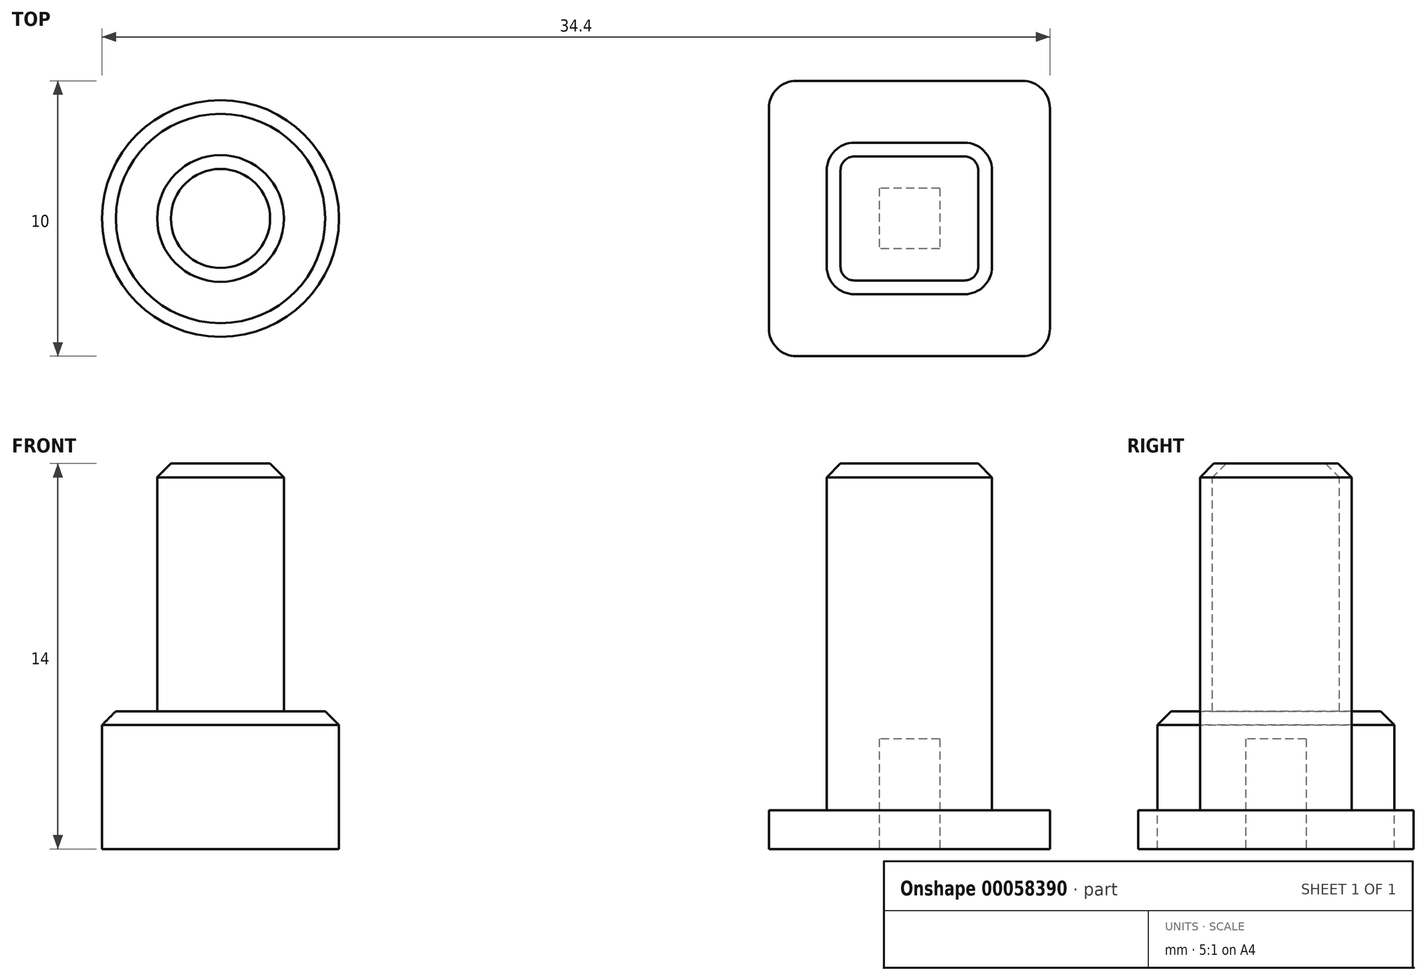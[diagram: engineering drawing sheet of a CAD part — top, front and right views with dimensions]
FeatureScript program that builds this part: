
annotation { "Feature Type Name" : "Feature", "Feature Type Description" : "" }
export const myFeature = defineFeature(function(context is Context, id is Id, definition is map)
    precondition{}
    {
        {
            var Q0;
            Q0=qCreatedBy(makeId("Front.planeOp"),FACE);
            var sketch = newSketch(context, id + "F0", { "sketchPlane" : qUnion([Q0])});
            skLineSegment(sketch, "E0", {"start": v(0, 0) * mm, "end": v(-4.3, 0) * mm});
            skLineSegment(sketch, "E1", {"start": v(-4.3, 5) * mm, "end": v(-2.3, 5) * mm});
            skLineSegment(sketch, "E2", {"start": v(-2.3, 5) * mm, "end": v(-2.3, 14) * mm});
            skLineSegment(sketch, "E3", {"start": v(-2.3, 14) * mm, "end": v(0, 14) * mm});
            skLineSegment(sketch, "E4", {"start": v(0, 14) * mm, "end": v(0, 0) * mm});
            skLineSegment(sketch, "E5", {"start": v(-4.3, 0) * mm, "end": v(-4.3, 5) * mm});
            skSolve(sketch);
        }
        {
            var Q0;
            Q0=makeQuery(id+"F0.imprint","IMPRINT",FACE,{"disambiguationData":[TD([[makeQuery(id+"F0.imprint","IMPRINT",EDGE,{"derivedFrom":sQuery(id+"F0.wireOp",EDGE,"E0")}),-1.0]])]});
            var Q1;
            Q1=sQuery(id+"F0.wireOp",EDGE,"E4");
            revolve(context, id + "F1", {"entities" : qUnion([Q0]), "axis" : qUnion([Q1]), "revolveType" : RevolveType.FULL});
        }
        {
            var Q0;
            Q0=makeQuery(id+"F1.opRevolve","SWEPT_EDGE",EDGE,{"disambiguationData":[OSD([sQuery(id+"F0.wireOp",EDGE,"E1"),sQuery(id+"F0.wireOp",EDGE,"E5")])]});
            var Q1;
            Q1=makeQuery(id+"F1.opRevolve","SWEPT_EDGE",EDGE,{"disambiguationData":[OSD([sQuery(id+"F0.wireOp",EDGE,"E2"),sQuery(id+"F0.wireOp",EDGE,"E3")])]});
            chamfer(context, id + "F2", {"entities" : qUnion([Q0, Q1]), "width" : 0.5 * mm, "tangentPropagation" : true});
        }
        {
            var Q0;
            Q0=qCreatedBy(makeId("Top.planeOp"),FACE);
            var sketch = newSketch(context, id + "F3", { "sketchPlane" : qUnion([Q0])});
            skLineSegment(sketch, "E6.rect.bottom", {"start": v(26.1, 1.1) * mm, "end": v(23.9, 1.1) * mm});
            skLineSegment(sketch, "E6.rect.top", {"start": v(26.1, -1.1) * mm, "end": v(23.9, -1.1) * mm});
            skLineSegment(sketch, "E6.rect.left", {"start": v(26.1, 1.1) * mm, "end": v(26.1, -1.1) * mm});
            skLineSegment(sketch, "E6.rect.right", {"start": v(23.9, 1.1) * mm, "end": v(23.9, -1.1) * mm});
            skPoint(sketch, "E6.rect.middle", {"position": v(25, 0) * mm});
            skLineSegment(sketch, "E7.rect.bottom", {"start": v(22, 2.75) * mm, "end": v(28, 2.75) * mm});
            skLineSegment(sketch, "E7.rect.top", {"start": v(22, -2.75) * mm, "end": v(28, -2.75) * mm});
            skLineSegment(sketch, "E7.rect.left", {"start": v(22, 2.75) * mm, "end": v(22, -2.75) * mm});
            skLineSegment(sketch, "E7.rect.right", {"start": v(28, 2.75) * mm, "end": v(28, -2.75) * mm});
            skLineSegment(sketch, "E8.rect.bottom", {"start": v(19.9, 5) * mm, "end": v(30.1, 5) * mm});
            skLineSegment(sketch, "E8.rect.top", {"start": v(19.9, -5) * mm, "end": v(30.1, -5) * mm});
            skLineSegment(sketch, "E8.rect.left", {"start": v(19.9, 5) * mm, "end": v(19.9, -5) * mm});
            skLineSegment(sketch, "E8.rect.right", {"start": v(30.1, 5) * mm, "end": v(30.1, -5) * mm});
            skSolve(sketch);
        }
        {
            var Q0;
            Q0=makeQuery(id+"F3.imprint","IMPRINT",FACE,{"disambiguationData":[TD([[makeQuery(id+"F3.imprint","IMPRINT",EDGE,{"derivedFrom":sQuery(id+"F3.wireOp",EDGE,"E6.rect.bottom")}),1.0]])]});
            var Q1;
            Q1=makeQuery(id+"F3.imprint","IMPRINT",FACE,{"disambiguationData":[TD([[makeQuery(id+"F3.imprint","IMPRINT",EDGE,{"derivedFrom":sQuery(id+"F3.wireOp",EDGE,"E6.rect.bottom")}),-1.0]])]});
            var Q2;
            Q2=makeQuery(id+"F1.opRevolve","SWEPT_FACE",FACE,{"disambiguationData":[OSD([sQuery(id+"F0.wireOp",EDGE,"E3")])]});
            extrude(context, id + "F4", {"entities" : qUnion([Q0, Q1]), "endBound" : BoundingType.UP_TO_SURFACE, "endBoundEntityFace" : qUnion([Q2]), "depth" : 25 * mm});
        }
        {
            var Q0;
            Q0=makeQuery(id+"F3.imprint","IMPRINT",FACE,{"disambiguationData":[TD([[makeQuery(id+"F3.imprint","IMPRINT",EDGE,{"derivedFrom":sQuery(id+"F3.wireOp",EDGE,"E7.rect.bottom")}),1.0]])]});
            extrude(context, id + "F5", {"entities" : qUnion([Q0]), "operationType" : NewBodyOperationType.ADD, "depth" : 1 * mm});
        }
        {
            var Q0;
            Q0=makeQuery(id+"F4.opExtrude","SWEPT_EDGE",EDGE,{"disambiguationData":[OSD([sQuery(id+"F3.wireOp",EDGE,"E7.rect.top"),sQuery(id+"F3.wireOp",EDGE,"E7.rect.left")])]});
            var Q1;
            Q1=makeQuery(id+"F4.opExtrude","SWEPT_EDGE",EDGE,{"disambiguationData":[OSD([sQuery(id+"F3.wireOp",EDGE,"E7.rect.top"),sQuery(id+"F3.wireOp",EDGE,"E7.rect.right")])]});
            var Q2;
            Q2=makeQuery(id+"F4.opExtrude","SWEPT_EDGE",EDGE,{"disambiguationData":[OSD([sQuery(id+"F3.wireOp",EDGE,"E7.rect.bottom"),sQuery(id+"F3.wireOp",EDGE,"E7.rect.right")])]});
            var Q3;
            Q3=makeQuery(id+"F4.opExtrude","SWEPT_EDGE",EDGE,{"disambiguationData":[OSD([sQuery(id+"F3.wireOp",EDGE,"E7.rect.bottom"),sQuery(id+"F3.wireOp",EDGE,"E7.rect.left")])]});
            var Q4;
            Q4=makeQuery(id+"F5.opExtrude","SWEPT_EDGE",EDGE,{"disambiguationData":[OSD([sQuery(id+"F3.wireOp",EDGE,"E8.rect.top"),sQuery(id+"F3.wireOp",EDGE,"E8.rect.right")])]});
            var Q5;
            Q5=makeQuery(id+"F5.opExtrude","SWEPT_EDGE",EDGE,{"disambiguationData":[OSD([sQuery(id+"F3.wireOp",EDGE,"E8.rect.top"),sQuery(id+"F3.wireOp",EDGE,"E8.rect.left")])]});
            var Q6;
            Q6=makeQuery(id+"F5.opExtrude","SWEPT_EDGE",EDGE,{"disambiguationData":[OSD([sQuery(id+"F3.wireOp",EDGE,"E8.rect.bottom"),sQuery(id+"F3.wireOp",EDGE,"E8.rect.right")])]});
            var Q7;
            Q7=makeQuery(id+"F5.opExtrude","SWEPT_EDGE",EDGE,{"disambiguationData":[OSD([sQuery(id+"F3.wireOp",EDGE,"E8.rect.bottom"),sQuery(id+"F3.wireOp",EDGE,"E8.rect.left")])]});
            fillet(context, id + "F6", {"entities" : qUnion([Q0, Q1, Q2, Q3, Q4, Q5, Q6, Q7]), "radius" : 1 * mm, "tangentPropagation" : true, "allowEdgeOverflow" : false});
        }
        {
            var Q0;
            Q0=makeQuery(id+"F4.opExtrude","CAP_FACE",FACE,{"disambiguationData":[OSD([sQuery(id+"F3.wireOp",EDGE,"E7.rect.bottom"),sQuery(id+"F3.wireOp",EDGE,"E7.rect.top"),sQuery(id+"F3.wireOp",EDGE,"E7.rect.left"),sQuery(id+"F3.wireOp",EDGE,"E7.rect.right")])],"isStart":false});
            chamfer(context, id + "F7", {"entities" : qUnion([Q0]), "width" : 0.5 * mm, "tangentPropagation" : true});
        }
        {
            var Q0;
            Q0=makeQuery(id+"F3.imprint","IMPRINT",FACE,{"disambiguationData":[TD([[makeQuery(id+"F3.imprint","IMPRINT",EDGE,{"derivedFrom":sQuery(id+"F3.wireOp",EDGE,"E6.rect.bottom")}),1.0]])]});
            extrude(context, id + "F8", {"entities" : qUnion([Q0]), "operationType" : NewBodyOperationType.REMOVE, "depth" : 4 * mm});
        }
        {
            var Q0;
            Q0=makeQuery(id+"F5.opExtrude","CAP_FACE",FACE,{"disambiguationData":[OSD([sQuery(id+"F3.wireOp",EDGE,"E7.rect.bottom"),sQuery(id+"F3.wireOp",EDGE,"E7.rect.top"),sQuery(id+"F3.wireOp",EDGE,"E7.rect.left"),sQuery(id+"F3.wireOp",EDGE,"E7.rect.right"),sQuery(id+"F3.wireOp",EDGE,"E8.rect.bottom"),sQuery(id+"F3.wireOp",EDGE,"E8.rect.top"),sQuery(id+"F3.wireOp",EDGE,"E8.rect.left"),sQuery(id+"F3.wireOp",EDGE,"E8.rect.right")])],"isStart":false});
            var Q1;
            Q1=makeQuery(id+"F1.opRevolve","SWEPT_FACE",FACE,{"disambiguationData":[OSD([sQuery(id+"F0.wireOp",EDGE,"E1")])]});
            extrude(context, id + "F9", {"entities" : qUnion([Q0]), "operationType" : NewBodyOperationType.ADD, "endBound" : BoundingType.UP_TO_SURFACE, "endBoundEntityFace" : qUnion([Q1]), "depth" : 25 * mm});
        }
        {
            var Q0;
            Q0=makeQuery(id+"F9.opExtrude","CAP_FACE",FACE,{"disambiguationData":[OSD([sQuery(id+"F3.wireOp",EDGE,"E7.rect.bottom"),sQuery(id+"F3.wireOp",EDGE,"E7.rect.top"),sQuery(id+"F3.wireOp",EDGE,"E7.rect.left"),sQuery(id+"F3.wireOp",EDGE,"E7.rect.right"),sQuery(id+"F3.wireOp",EDGE,"E8.rect.bottom"),sQuery(id+"F3.wireOp",EDGE,"E8.rect.top"),sQuery(id+"F3.wireOp",EDGE,"E8.rect.left"),sQuery(id+"F3.wireOp",EDGE,"E8.rect.right")])],"isStart":false});
            extrude(context, id + "F10", {"entities" : qUnion([Q0]), "operationType" : NewBodyOperationType.REMOVE, "oppositeDirection" : true, "depth" : 3.6 * mm});
        }
    });
